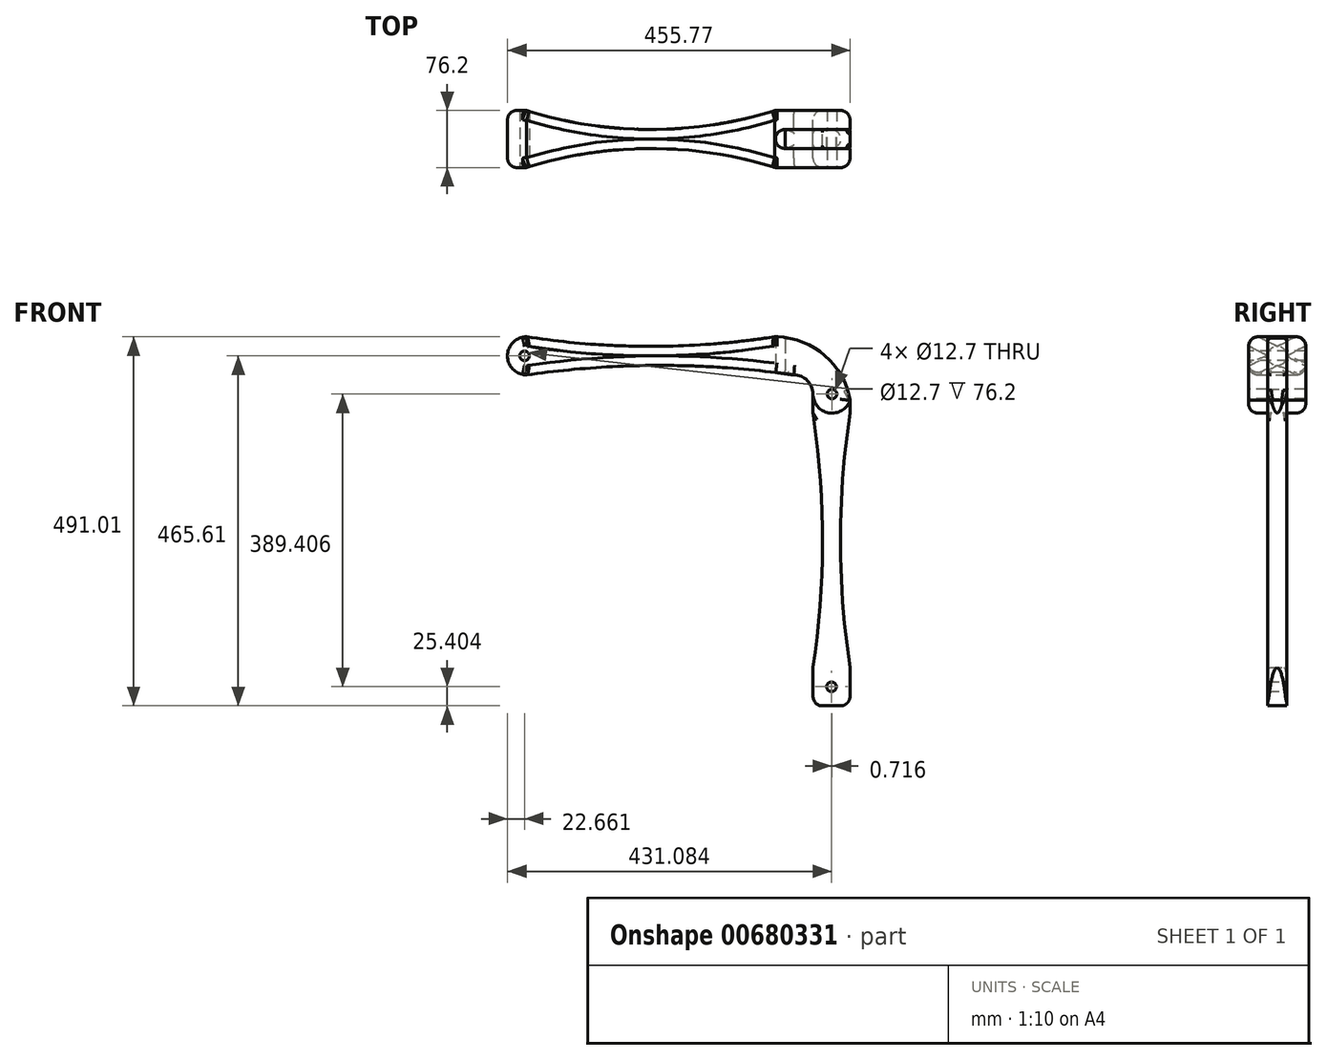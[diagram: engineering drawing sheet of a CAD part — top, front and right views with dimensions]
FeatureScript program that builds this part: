
annotation { "Feature Type Name" : "Feature", "Feature Type Description" : "" }
export const myFeature = defineFeature(function(context is Context, id is Id, definition is map)
    precondition{}
    {
        {
            var Q0;
            Q0=qCreatedBy(makeId("Front.planeOp"),FACE);
            var sketch = newSketch(context, id + "F0", { "sketchPlane" : qUnion([Q0])});
            skLineSegment(sketch, "E0.bottom", {"start": v(0, 25.4) * mm, "end": v(127, 25.4) * mm, "construction": true});
            skLineSegment(sketch, "E0.top", {"start": v(-203.2, -25.4) * mm, "end": v(152.4, -25.4) * mm, "construction": true});
            skLineSegment(sketch, "E0.left", {"start": v(-228.6, 0) * mm, "end": v(-228.6, 0) * mm});
            skLineSegment(sketch, "E0.right", {"start": v(228.6, -25.4) * mm, "end": v(228.6, -76.2) * mm});
            skPoint(sketch, "E1", {"position": v(-228.6, 0) * mm});
            skPoint(sketch, "E2", {"position": v(0, 25.4) * mm});
            skLineSegment(sketch, "E3.top", {"start": v(203.2, -76.2) * mm, "end": v(203.2, -76.2) * mm});
            skLineSegment(sketch, "E3.left", {"start": v(228.6, -25.4) * mm, "end": v(228.6, -50.8) * mm});
            skLineSegment(sketch, "E3.right", {"start": v(177.8, -50.8) * mm, "end": v(177.8, -50.8) * mm});
            skPoint(sketch, "E4.visualSharp", {"position": v(177.8, -76.2) * mm});
            skArc(sketch, "E4.filletArc", {"start": v(177.8, -50.8) * mm, "mid": v(185.24, -68.76) * mm, "end": v(203.2, -76.2) * mm});
            skPoint(sketch, "E5.visualSharp", {"position": v(228.6, -76.2) * mm});
            skArc(sketch, "E5.filletArc", {"start": v(203.2, -76.2) * mm, "mid": v(221.16, -68.76) * mm, "end": v(228.6, -50.8) * mm});
            skPoint(sketch, "E6.visualSharp", {"position": v(228.6, 25.4) * mm});
            skArc(sketch, "E6.filletArc", {"start": v(228.6, -76.2) * mm, "mid": v(198.84, -4.36) * mm, "end": v(127, 25.4) * mm});
            skPoint(sketch, "E7.visualSharp", {"position": v(177.8, -25.4) * mm});
            skArc(sketch, "E7.filletArc", {"start": v(177.8, -50.8) * mm, "mid": v(170.36, -32.84) * mm, "end": v(152.4, -25.4) * mm});
            skPoint(sketch, "E8.visualSharp", {"position": v(-228.6, -25.4) * mm});
            skArc(sketch, "E8.filletArc", {"start": v(-228.6, 0) * mm, "mid": v(-221.16, -17.96) * mm, "end": v(-203.2, -25.4) * mm});
            skPoint(sketch, "E9.visualSharp", {"position": v(-228.6, 25.4) * mm});
            skArc(sketch, "E9.filletArc", {"start": v(-203.2, 25.4) * mm, "mid": v(-221.16, 17.96) * mm, "end": v(-228.6, 0) * mm});
            skArc(sketch, "E10", {"start": v(-203.2, 25.4) * mm, "mid": v(-38.1, 12.7) * mm, "end": v(127, 25.4) * mm});
            skArc(sketch, "E11", {"start": v(152.4, -25.4) * mm, "mid": v(-25.4, -12.7) * mm, "end": v(-203.2, -25.4) * mm});
            skSolve(sketch);
        }
        {
            var Q0;
            Q0 = qSketchRegion(id + "F0", true);
            extrude(context, id + "F1", {"entities" : qUnion([Q0]), "depth" : 76.2 * mm, "offsetDistance" : 25.4 * mm});
        }
        {
            var Q0;
            Q0=makeQuery(id+"F1.opExtrude","CAP_FACE",FACE,{"disambiguationData":[OSD([sQuery(id+"F0.wireOp",EDGE,"E4.filletArc"),sQuery(id+"F0.wireOp",EDGE,"E5.filletArc"),sQuery(id+"F0.wireOp",EDGE,"E6.filletArc"),sQuery(id+"F0.wireOp",EDGE,"E7.filletArc"),sQuery(id+"F0.wireOp",EDGE,"E8.filletArc"),sQuery(id+"F0.wireOp",EDGE,"E9.filletArc"),sQuery(id+"F0.wireOp",EDGE,"E10"),sQuery(id+"F0.wireOp",EDGE,"E11")])],"isStart":false});
            var Q1;
            Q1=makeQuery(id+"F1.opExtrude","CAP_FACE",FACE,{"disambiguationData":[OSD([sQuery(id+"F0.wireOp",EDGE,"E4.filletArc"),sQuery(id+"F0.wireOp",EDGE,"E5.filletArc"),sQuery(id+"F0.wireOp",EDGE,"E6.filletArc"),sQuery(id+"F0.wireOp",EDGE,"E7.filletArc"),sQuery(id+"F0.wireOp",EDGE,"E8.filletArc"),sQuery(id+"F0.wireOp",EDGE,"E9.filletArc"),sQuery(id+"F0.wireOp",EDGE,"E10"),sQuery(id+"F0.wireOp",EDGE,"E11")])],"isStart":true});
            fillet(context, id + "F2", {"entities" : qUnion([Q0, Q1]), "radius" : 12.7 * mm, "tangentPropagation" : true, "allowEdgeOverflow" : false});
        }
        {
            var Q0;
            Q0=makeQuery(id+"F1.opExtrude","SWEPT_BODY",BODY,{"disambiguationData":[OSD([sQuery(id+"F0.wireOp",EDGE,"E0.right"),sQuery(id+"F0.wireOp",EDGE,"E5.filletArc"),sQuery(id+"F0.wireOp",EDGE,"E6.filletArc")])]});
            deleteBodies(context, id + "F3", {"entities" : qUnion([Q0])});
        }
        {
            var Q0;
            Q0=qCreatedBy(makeId("Top.planeOp"),FACE);
            cPlane(context, id + "F4", {"entities" : qUnion([Q0]), "cplaneType" : CPlaneType.OFFSET, "offset" : 25.4 * mm, "width" : 152.4 * mm, "height" : 152.4 * mm});
        }
        {
            var Q0;
            Q0=qCreatedBy(id+"F4.planeOp",FACE);
            var sketch = newSketch(context, id + "F5", { "sketchPlane" : qUnion([Q0])});
            skLineSegment(sketch, "E12", {"start": v(127.94, 0) * mm, "end": v(127.94, -76.2) * mm, "construction": true});
            skLineSegment(sketch, "E13.bottom", {"start": v(127.94, -25.4) * mm, "end": v(227.17, -25.4) * mm});
            skLineSegment(sketch, "E13.top", {"start": v(127.94, -50.8) * mm, "end": v(227.17, -50.8) * mm});
            skLineSegment(sketch, "E13.left", {"start": v(127.94, -25.4) * mm, "end": v(127.94, -50.8) * mm});
            skLineSegment(sketch, "E13.right", {"start": v(227.17, -25.4) * mm, "end": v(227.17, -50.8) * mm});
            skPoint(sketch, "E14", {"position": v(127.94, -38.1) * mm});
            skSolve(sketch);
        }
        {
            var Q0;
            Q0 = qSketchRegion(id + "F5", true);
            extrude(context, id + "F6", {"entities" : qUnion([Q0]), "operationType" : NewBodyOperationType.REMOVE, "oppositeDirection" : true, "depth" : 101.6 * mm, "offsetDistance" : 25.4 * mm});
        }
        {
            var Q0;
            Q0=makeQuery(id+"F6.boolean.opBoolean","COPY",EDGE,{"derivedFrom":makeQuery(id+"F6.opExtrude","SWEPT_EDGE",EDGE,{"disambiguationData":[OSD([sQuery(id+"F5.wireOp",EDGE,"E13.top"),sQuery(id+"F5.wireOp",EDGE,"E13.left")])]})});
            var Q1;
            Q1=makeQuery(id+"F6.boolean.opBoolean","COPY",EDGE,{"derivedFrom":makeQuery(id+"F6.opExtrude","SWEPT_EDGE",EDGE,{"disambiguationData":[OSD([sQuery(id+"F5.wireOp",EDGE,"E13.bottom"),sQuery(id+"F5.wireOp",EDGE,"E13.left")])]})});
            fillet(context, id + "F7", {"entities" : qUnion([Q0, Q1]), "radius" : 12.7 * mm, "tangentPropagation" : true, "allowEdgeOverflow" : false});
        }
        {
            var Q0;
            Q0=qCreatedBy(id+"F4.planeOp",FACE);
            var sketch = newSketch(context, id + "F8", { "sketchPlane" : qUnion([Q0])});
            skArc(sketch, "E15", {"start": v(-204, 0) * mm, "mid": v(-38.03, -25.4) * mm, "end": v(127.94, 0) * mm});
            skLineSegment(sketch, "E16", {"start": v(-203.2, -38.1) * mm, "end": v(90.23, -38.1) * mm, "construction": true});
            skLineSegment(sketch, "E17", {"start": v(-204, 0) * mm, "end": v(127.94, 0) * mm});
            skArc(sketch, "E18.MirrorCS", {"start": v(-204, -76.2) * mm, "mid": v(-38.03, -50.8) * mm, "end": v(127.94, -76.2) * mm});
            skLineSegment(sketch, "E19.MirrorCS", {"start": v(-204, -76.2) * mm, "end": v(127.94, -76.2) * mm});
            skSolve(sketch);
        }
        {
            var Q0;
            Q0 = qSketchRegion(id + "F8", true);
            extrude(context, id + "F9", {"entities" : qUnion([Q0]), "operationType" : NewBodyOperationType.REMOVE, "oppositeDirection" : true, "depth" : 89.66 * mm, "offsetDistance" : 25.4 * mm});
        }
        {
            var Q0;
            Q0=makeQuery(id+"F9.boolean.opBoolean","COPY",FACE,{"derivedFrom":makeQuery(id+"F9.opExtrude","SWEPT_FACE",FACE,{"disambiguationData":[OSD([sQuery(id+"F8.wireOp",EDGE,"E18.MirrorCS")])]})});
            var Q1;
            Q1=makeQuery(id+"F9.boolean.opBoolean","COPY",FACE,{"derivedFrom":makeQuery(id+"F9.opExtrude","SWEPT_FACE",FACE,{"disambiguationData":[OSD([sQuery(id+"F8.wireOp",EDGE,"E15")])]})});
            fillet(context, id + "F10", {"entities" : qUnion([Q0, Q1]), "radius" : 12.7 * mm, "tangentPropagation" : true, "allowEdgeOverflow" : false});
        }
        {
            var Q0;
            {var subQ0=sQuery(id+"F0.wireOp",EDGE,"E9.filletArc");var subQ1=sQuery(id+"F0.wireOp",EDGE,"E8.filletArc");Q0=makeQuery(id+"F9.boolean.opBoolean","SPLIT",FACE,{"disambiguationData":[TD([makeQuery(id+"F2.opFillet","BLEND_FACE",FACE,{"disambiguationData":[OSD([subQ1,subQ0]),TDD([makeQuery(id+"F1.opExtrude","CAP_EDGE",EDGE,{"disambiguationData":[OSD([subQ1,subQ0])],"isStart":false})])]})])],"derivedFrom":makeQuery(id+"F1.opExtrude","CAP_FACE",FACE,{"disambiguationData":[OSD([sQuery(id+"F0.wireOp",EDGE,"E4.filletArc"),sQuery(id+"F0.wireOp",EDGE,"E5.filletArc"),sQuery(id+"F0.wireOp",EDGE,"E6.filletArc"),sQuery(id+"F0.wireOp",EDGE,"E7.filletArc"),subQ1,subQ0,sQuery(id+"F0.wireOp",EDGE,"E10"),sQuery(id+"F0.wireOp",EDGE,"E11")])],"isStart":false})});}
            var sketch = newSketch(context, id + "F11", { "sketchPlane" : qUnion([Q0])});
            skCircle(sketch, "E20", {"center": v(-205.94, 0) * mm, "radius": 6.35 * mm});
            skCircle(sketch, "E21", {"center": v(203.2, -50.8) * mm, "radius": 6.35 * mm});
            skSolve(sketch);
        }
        {
            var Q0;
            Q0 = qSketchRegion(id + "F11", true);
            extrude(context, id + "F12", {"entities" : qUnion([Q0]), "operationType" : NewBodyOperationType.REMOVE, "endBound" : BoundingType.THROUGH_ALL, "oppositeDirection" : true, "depth" : 25.4 * mm, "offsetDistance" : 25.4 * mm});
        }
        {
            var Q0;
            Q0=makeQuery(id+"F6.boolean.opBoolean","COPY",FACE,{"derivedFrom":makeQuery(id+"F6.opExtrude","SWEPT_FACE",FACE,{"disambiguationData":[OSD([sQuery(id+"F5.wireOp",EDGE,"E13.bottom")])]})});
            var sketch = newSketch(context, id + "F13", { "sketchPlane" : qUnion([Q0])});
            skArc(sketch, "E22", {"start": v(227.17, -59.2) * mm, "mid": v(197.63, -3.17) * mm, "end": v(140.64, 24.48) * mm});
            skLineSegment(sketch, "E23", {"start": v(140.64, 24.48) * mm, "end": v(140.64, -23.77) * mm});
            skLineSegment(sketch, "E24", {"start": v(140.64, -23.77) * mm, "end": v(152.4, -25.4) * mm});
            skArc(sketch, "E25", {"start": v(177.8, -50.8) * mm, "mid": v(170.36, -32.84) * mm, "end": v(152.4, -25.4) * mm});
            skLineSegment(sketch, "E26.top", {"start": v(190.5, -465.6) * mm, "end": v(214.47, -465.6) * mm});
            skLineSegment(sketch, "E26.left", {"start": v(177.8, -50.8) * mm, "end": v(177.8, -452.9) * mm, "construction": true});
            skLineSegment(sketch, "E26.right", {"start": v(227.17, -59.2) * mm, "end": v(227.17, -452.9) * mm, "construction": true});
            skPoint(sketch, "E27.oppositeSnap0", {"position": v(198.94, -75.84) * mm});
            skLineSegment(sketch, "E27.bottom", {"start": v(177.8, -50.8) * mm, "end": v(227.17, -50.8) * mm, "construction": true});
            skLineSegment(sketch, "E27.top", {"start": v(177.8, -75.84) * mm, "end": v(227.17, -75.84) * mm, "construction": true});
            skLineSegment(sketch, "E27.left", {"start": v(177.8, -50.8) * mm, "end": v(177.8, -75.84) * mm});
            skLineSegment(sketch, "E27.right", {"start": v(227.17, -59.2) * mm, "end": v(227.17, -75.84) * mm});
            skLineSegment(sketch, "E28", {"start": v(177.8, -465.6) * mm, "end": v(177.8, -414.8) * mm});
            skLineSegment(sketch, "E29", {"start": v(177.8, -414.8) * mm, "end": v(227.17, -414.8) * mm, "construction": true});
            skLineSegment(sketch, "E30", {"start": v(227.17, -414.8) * mm, "end": v(227.17, -465.6) * mm});
            skArc(sketch, "E31", {"start": v(177.8, -414.8) * mm, "mid": v(190.5, -245.32) * mm, "end": v(177.8, -75.84) * mm});
            skLineSegment(sketch, "E32", {"start": v(202.48, -414.8) * mm, "end": v(202.48, -174.67) * mm, "construction": true});
            skArc(sketch, "E33.MirrorCS", {"start": v(227.17, -414.8) * mm, "mid": v(214.47, -245.32) * mm, "end": v(227.17, -75.84) * mm});
            skPoint(sketch, "E34.visualSharp", {"position": v(177.8, -465.6) * mm});
            skArc(sketch, "E34.filletArc", {"start": v(177.8, -452.9) * mm, "mid": v(181.52, -461.89) * mm, "end": v(190.5, -465.6) * mm});
            skPoint(sketch, "E35.visualSharp", {"position": v(227.17, -465.6) * mm});
            skArc(sketch, "E35.filletArc", {"start": v(214.47, -465.6) * mm, "mid": v(223.45, -461.89) * mm, "end": v(227.17, -452.9) * mm});
            skCircle(sketch, "E36", {"center": v(203.2, -50.8) * mm, "radius": 6.35 * mm});
            skLineSegment(sketch, "E37", {"start": v(202.48, -414.8) * mm, "end": v(202.48, -465.6) * mm, "construction": true});
            skCircle(sketch, "E38", {"center": v(202.48, -440.2) * mm, "radius": 6.35 * mm});
            skSolve(sketch);
        }
        {
            var Q0;
            Q0 = qSketchRegion(id + "F13", true);
            extrude(context, id + "F14", {"entities" : qUnion([Q0]), "depth" : 25.4 * mm, "offsetDistance" : 25.4 * mm});
        }
        {
            var Q0;
            Q0=makeQuery(id+"F14.opExtrude","CAP_EDGE",EDGE,{"disambiguationData":[OSD([sQuery(id+"F13.wireOp",EDGE,"E33.MirrorCS")])],"isStart":false});
            var Q1;
            Q1=makeQuery(id+"F14.opExtrude","CAP_EDGE",EDGE,{"disambiguationData":[OSD([sQuery(id+"F13.wireOp",EDGE,"E33.MirrorCS")])],"isStart":true});
            fillet(context, id + "F15", {"entities" : qUnion([Q0, Q1]), "radius" : 12.7 * mm, "tangentPropagation" : true, "allowEdgeOverflow" : false});
        }
        {
            var Q0;
            Q0=makeQuery(id+"F14.opExtrude","CAP_EDGE",EDGE,{"disambiguationData":[OSD([sQuery(id+"F13.wireOp",EDGE,"E31")])],"isStart":false});
            var Q1;
            Q1=makeQuery(id+"F14.opExtrude","CAP_EDGE",EDGE,{"disambiguationData":[OSD([sQuery(id+"F13.wireOp",EDGE,"E31")])],"isStart":true});
            fillet(context, id + "F16", {"entities" : qUnion([Q0, Q1]), "radius" : 3.8 * mm, "tangentPropagation" : true, "allowEdgeOverflow" : false});
        }
        {
            var Q0;
            Q0=makeQuery(id+"F14.opExtrude","SWEPT_EDGE",EDGE,{"disambiguationData":[OSD([sQuery(id+"F13.wireOp",EDGE,"E22"),sQuery(id+"F13.wireOp",EDGE,"E23")])]});
            var Q1;
            Q1=makeQuery(id+"F14.opExtrude","CAP_EDGE",EDGE,{"disambiguationData":[OSD([sQuery(id+"F13.wireOp",EDGE,"E22")])],"isStart":true});
            var Q2;
            Q2=makeQuery(id+"F14.opExtrude","CAP_EDGE",EDGE,{"disambiguationData":[OSD([sQuery(id+"F13.wireOp",EDGE,"E22")])],"isStart":false});
            var Q3;
            Q3=makeQuery(id+"F14.opExtrude","SWEPT_FACE",FACE,{"disambiguationData":[OSD([sQuery(id+"F13.wireOp",EDGE,"E23")])]});
            var Q4;
            Q4=makeQuery(id+"F14.opExtrude","SWEPT_FACE",FACE,{"disambiguationData":[OSD([sQuery(id+"F13.wireOp",EDGE,"E25")])]});
            fillet(context, id + "F17", {"entities" : qUnion([Q0, Q1, Q2, Q3, Q4]), "radius" : 5.08 * mm, "tangentPropagation" : true, "allowEdgeOverflow" : false});
        }
    });
